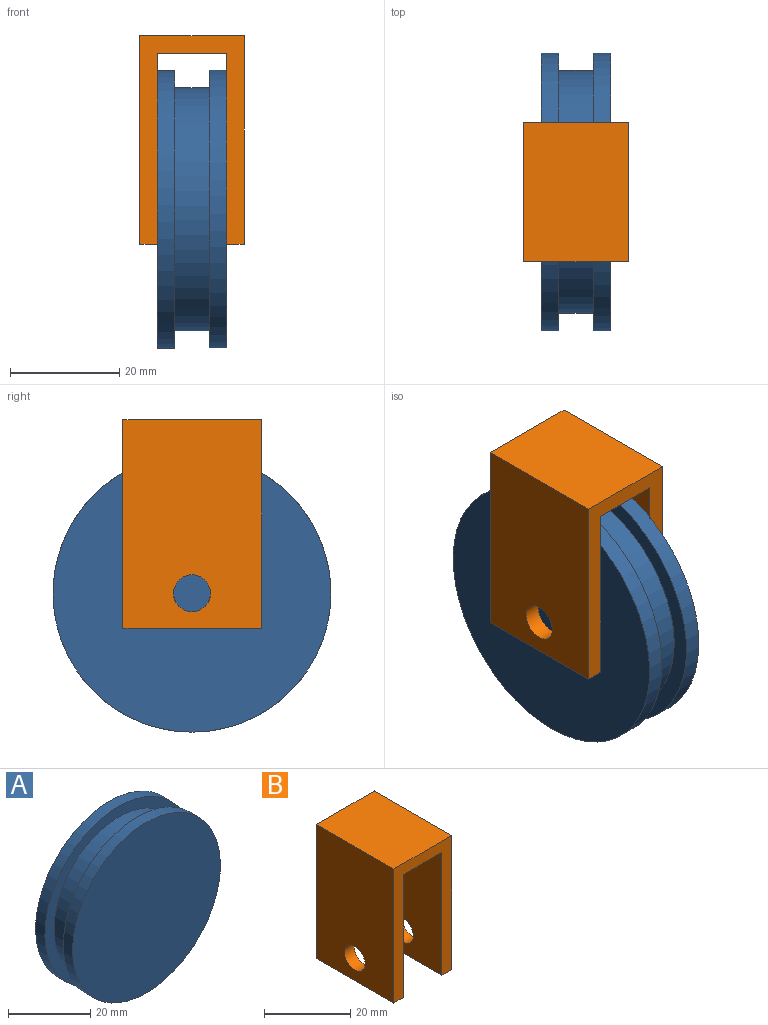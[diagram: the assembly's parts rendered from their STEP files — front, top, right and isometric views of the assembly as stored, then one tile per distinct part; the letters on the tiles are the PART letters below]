
ASSEMBLY  parts=2 mates=1
PART A: 7 faces, bbox 50.8x12.7x50.8 mm
  f0: cylinder r=25.4mm len=50.8mm, axis (0,1,0), area 506.7mm2, adj f1,f2
  f1: plane 50.8x50.8mm, normal (0,-1,0), area 2026.8mm2, adj f0
  f2: plane 50.8x50.8mm, normal (0,1,0), area 475mm2, adj f0,f3
  f3: cylinder r=22.23mm len=44.45mm, axis (0,-1,0), area 886.7mm2, adj f2,f6
  f4: cylinder r=25.4mm len=50.8mm, axis (0,-1,0), area 506.7mm2, adj f5,f6
  f5: plane 50.8x50.8mm, normal (0,1,0), area 2026.8mm2, adj f4
  f6: plane 50.8x50.8mm, normal (0,-1,0), area 475mm2, adj f3,f4
PART B: 12 faces, bbox 19.1x25.4x38.1 mm
  f0: plane 34.93x25.4mm, normal (1,0,0), area 851.2mm2, adj f1,f7,f8,f9,f10
  f1: plane 25.4x12.7mm, normal (0,0,-1), area 322.6mm2, adj f0,f2,f8,f9
  f2: plane 34.93x25.4mm, normal (-1,0,0), area 851.2mm2, adj f1,f3,f8,f9,f11
  f3: plane 25.4x3.18mm, normal (0,0,-1), area 80.6mm2, adj f2,f4,f8,f9
  f4: plane 38.1x25.4mm, normal (1,0,0), area 931.9mm2, adj f3,f5,f8,f9,f11
  f5: plane 25.4x19.05mm, normal (0,0,1), area 483.9mm2, adj f4,f6,f8,f9
  f6: plane 38.1x25.4mm, normal (-1,0,0), area 931.9mm2, adj f5,f7,f8,f9,f10
  f7: plane 25.4x3.18mm, normal (0,0,-1), area 80.6mm2, adj f0,f6,f8,f9
  f8: plane 38.1x19.05mm, normal (0,-1,0), area 282.3mm2, adj f0,f1,f2,f3,f4,f5,f6,f7
  f9: plane 38.1x19.05mm, normal (0,1,0), area 282.3mm2, adj f0,f1,f2,f3,f4,f5,f6,f7
  f10: cylinder r=3.38mm len=6.76mm, axis (-1,0,0), area 67.4mm2, adj f0,f6
  f11: cylinder r=3.38mm len=6.76mm, axis (-1,0,0), area 67.4mm2, adj f2,f4
PLACE A rot(axis=(0,0,-1),90deg) t=(-3.17,-12.62,-28.53)mm
PLACE B at identity
MATE fastened A.f0 <-> B.f10  axis (1,0,0) through (6.35,-12.62,-28.53)mm
